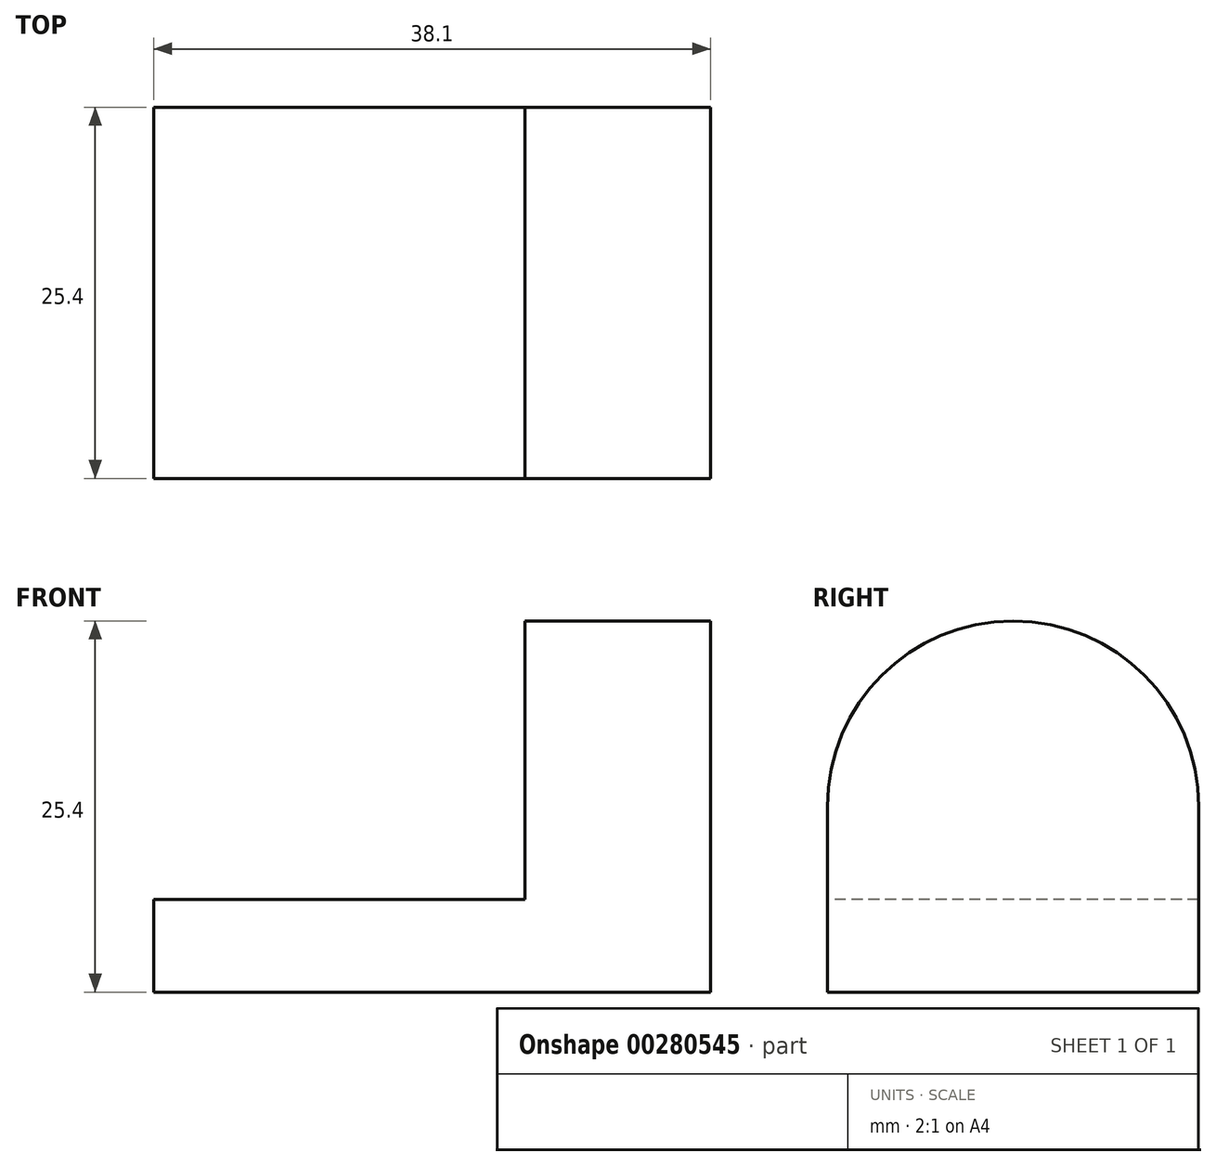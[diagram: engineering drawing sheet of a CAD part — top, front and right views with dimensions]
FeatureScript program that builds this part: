
annotation { "Feature Type Name" : "Feature", "Feature Type Description" : "" }
export const myFeature = defineFeature(function(context is Context, id is Id, definition is map)
    precondition{}
    {
        {
            var Q0;
            Q0=qCreatedBy(makeId("Right.planeOp"),FACE);
            var sketch = newSketch(context, id + "F0", { "sketchPlane" : qUnion([Q0])});
            skLineSegment(sketch, "E0", {"start": v(0, 0) * mm, "end": v(0, -6.35) * mm});
            skLineSegment(sketch, "E1", {"start": v(0, -6.35) * mm, "end": v(25.4, -6.35) * mm});
            skLineSegment(sketch, "E2", {"start": v(25.4, -6.35) * mm, "end": v(25.4, 0) * mm});
            skLineSegment(sketch, "E3", {"start": v(25.4, 0) * mm, "end": v(0, 0) * mm});
            skLineSegment(sketch, "E4", {"start": v(25.4, 0) * mm, "end": v(25.4, 6.35) * mm});
            skLineSegment(sketch, "E5", {"start": v(0, 0) * mm, "end": v(0, 6.35) * mm});
            skArc(sketch, "E6", {"start": v(25.4, 6.35) * mm, "mid": v(12.7, 19.05) * mm, "end": v(0, 6.35) * mm});
            skSolve(sketch);
        }
        {
            var Q0;
            Q0 = qSketchRegion(id + "F0", true);
            extrude(context, id + "F1", {"entities" : qUnion([Q0]), "oppositeDirection" : true, "depth" : 38.1 * mm});
        }
        {
            var Q0;
            Q0=makeQuery(id+"F0.imprint","IMPRINT",FACE,{"disambiguationData":[TD([[makeQuery(id+"F0.imprint","IMPRINT",EDGE,{"derivedFrom":sQuery(id+"F0.wireOp",EDGE,"E3")}),-1.0]])]});
            extrude(context, id + "F2", {"entities" : qUnion([Q0]), "operationType" : NewBodyOperationType.REMOVE, "oppositeDirection" : true, "depth" : 38.1 * mm, "hasSecondDirection" : true, "secondDirectionOppositeDirection" : true, "secondDirectionDepth" : 12.7 * mm});
        }
    });
